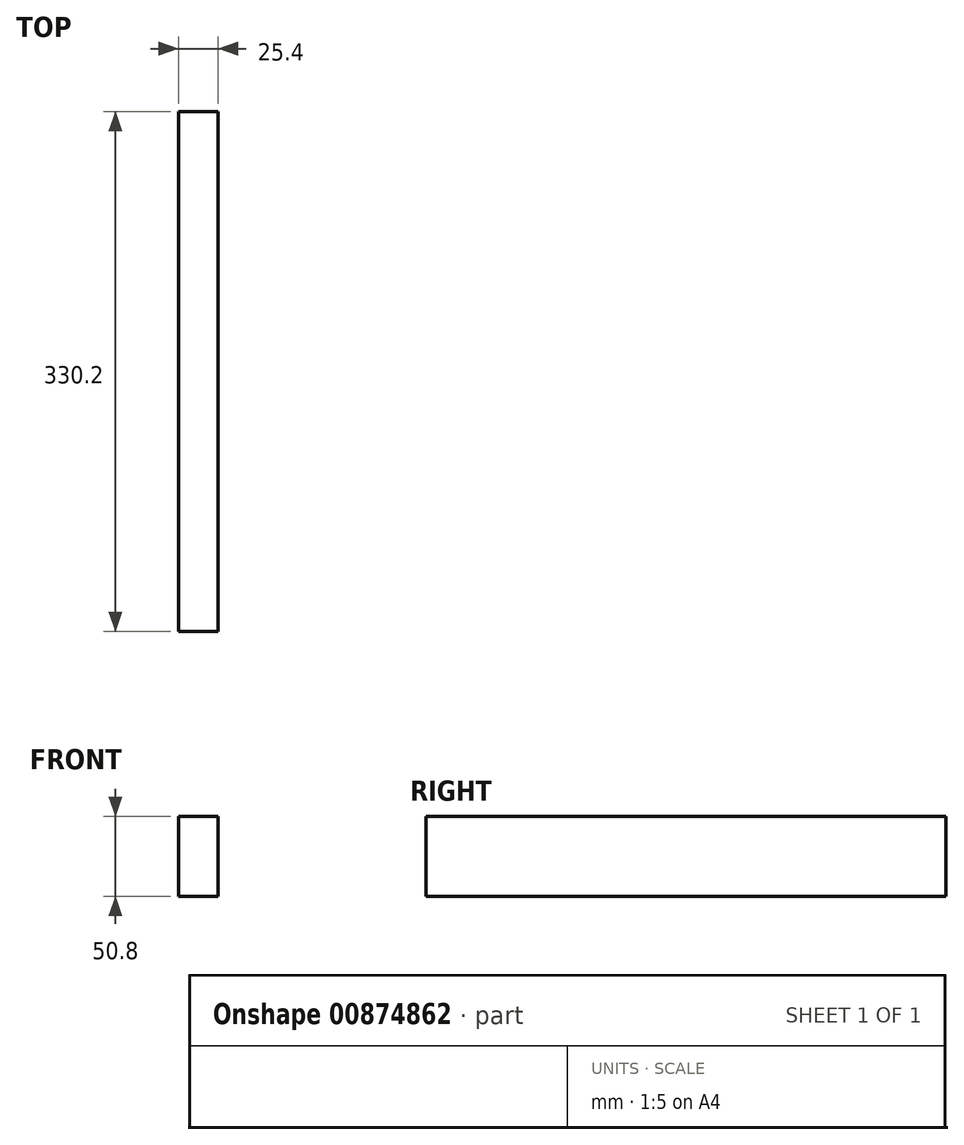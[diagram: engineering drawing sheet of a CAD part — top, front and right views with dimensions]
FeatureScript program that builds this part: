
annotation { "Feature Type Name" : "Feature", "Feature Type Description" : "" }
export const myFeature = defineFeature(function(context is Context, id is Id, definition is map)
    precondition{}
    {
        {
            var Q0;
            Q0=qCreatedBy(makeId("Front.planeOp"),FACE);
            var sketch = newSketch(context, id + "F0", { "sketchPlane" : qUnion([Q0])});
            skLineSegment(sketch, "E0", {"start": v(-56.99, 35.95) * mm, "end": v(-31.59, 35.95) * mm});
            skLineSegment(sketch, "E1", {"start": v(-31.59, 35.95) * mm, "end": v(-31.59, -14.85) * mm});
            skLineSegment(sketch, "E2", {"start": v(-31.59, -14.85) * mm, "end": v(-56.99, -14.85) * mm});
            skLineSegment(sketch, "E3", {"start": v(-56.99, -14.85) * mm, "end": v(-56.99, 35.95) * mm});
            skSolve(sketch);
        }
        {
            var Q0;
            Q0 = qSketchRegion(id + "F0", true);
            extrude(context, id + "F1", {"entities" : qUnion([Q0]), "depth" : 330.2 * mm, "offsetDistance" : 25.4 * mm});
        }
    });
